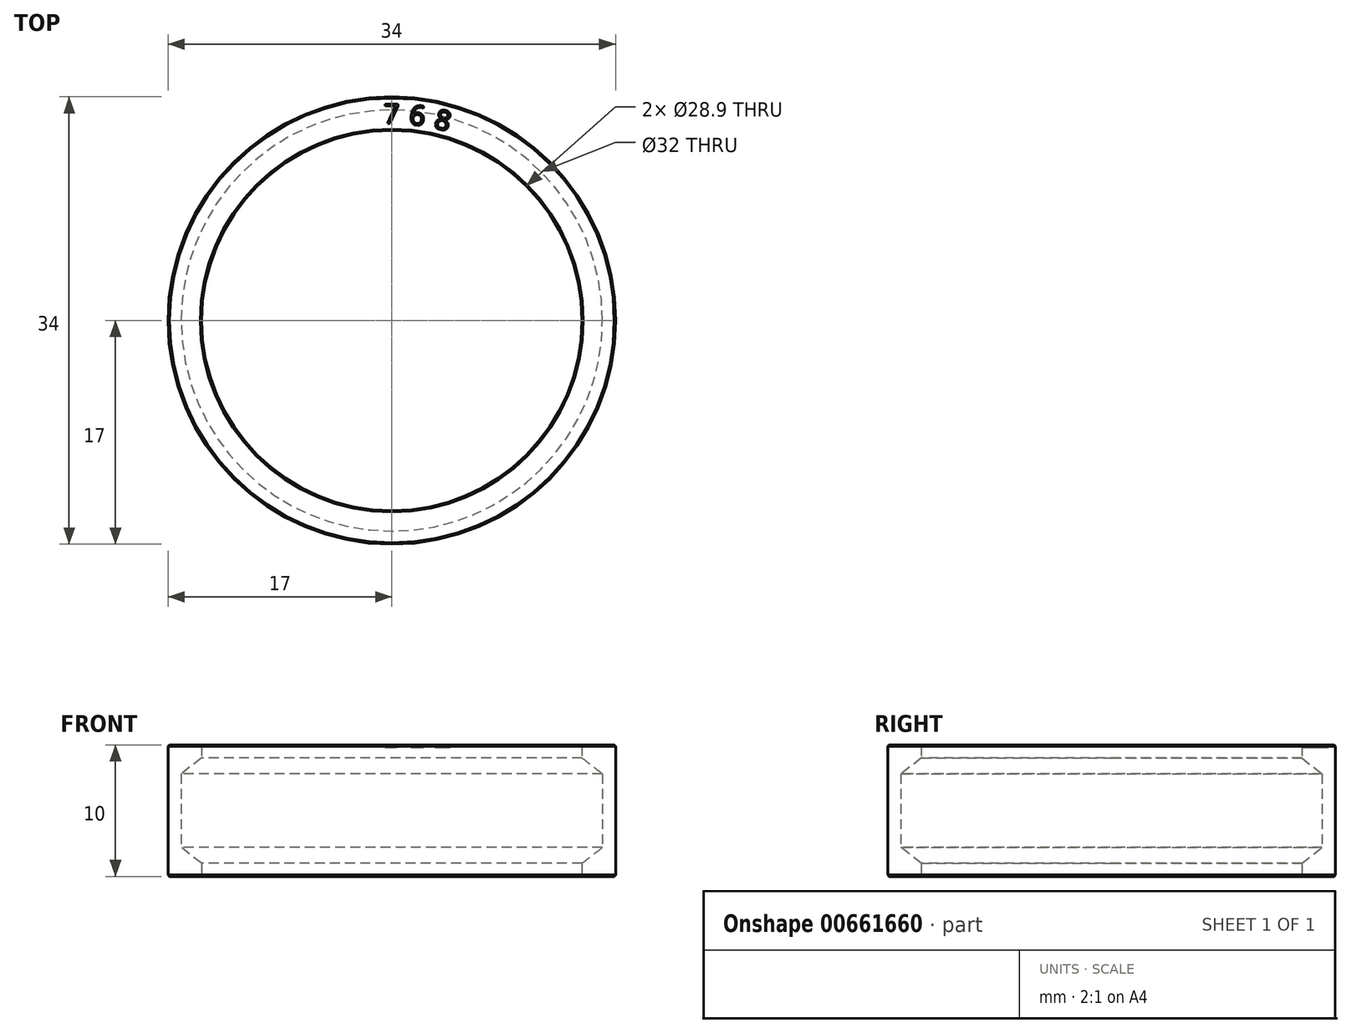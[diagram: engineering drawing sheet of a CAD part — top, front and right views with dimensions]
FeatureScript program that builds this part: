
annotation { "Feature Type Name" : "Feature", "Feature Type Description" : "" }
export const myFeature = defineFeature(function(context is Context, id is Id, definition is map)
    precondition{}
    {
        {
            var Q0;
            Q0=qCreatedBy(makeId("Top.planeOp"),FACE);
            var sketch = newSketch(context, id + "F0", { "sketchPlane" : qUnion([Q0])});
            skCircle(sketch, "E0", {"center": v(0, 0) * mm, "radius": 14.45 * mm});
            skCircle(sketch, "E1", {"center": v(0, 0) * mm, "radius": 17 * mm});
            skCircle(sketch, "E2", {"center": v(0, 0) * mm, "radius": 16 * mm});
            skSolve(sketch);
        }
        {
            var Q0;
            Q0=makeQuery(id+"F0.imprint","IMPRINT",FACE,{"disambiguationData":[TD([[makeQuery(id+"F0.imprint","IMPRINT",EDGE,{"derivedFrom":sQuery(id+"F0.wireOp",EDGE,"E0")}),-1.0]])]});
            var Q1;
            Q1=makeQuery(id+"F0.imprint","IMPRINT",FACE,{"disambiguationData":[TD([[makeQuery(id+"F0.imprint","IMPRINT",EDGE,{"derivedFrom":sQuery(id+"F0.wireOp",EDGE,"E1")}),1.0]])]});
            extrude(context, id + "F1", {"entities" : qUnion([Q0, Q1]), "endBound" : BoundingType.SYMMETRIC, "depth" : 10 * mm, "offsetDistance" : 25 * mm});
        }
        {
            var Q0;
            Q0=makeQuery(id+"F0.imprint","IMPRINT",FACE,{"disambiguationData":[TD([[makeQuery(id+"F0.imprint","IMPRINT",EDGE,{"derivedFrom":sQuery(id+"F0.wireOp",EDGE,"E0")}),-1.0]])]});
            var Q1;
            Q1=makeQuery(id+"F1.opExtrude","CAP_FACE",FACE,{"disambiguationData":[OSD([sQuery(id+"F0.wireOp",EDGE,"E0"),sQuery(id+"F0.wireOp",EDGE,"E1")])],"isStart":false});
            var Q2;
            Q2=makeQuery(id+"F1.opExtrude","CAP_FACE",FACE,{"disambiguationData":[OSD([sQuery(id+"F0.wireOp",EDGE,"E0"),sQuery(id+"F0.wireOp",EDGE,"E1")])],"isStart":true});
            extrude(context, id + "F2", {"entities" : qUnion([Q0]), "operationType" : NewBodyOperationType.REMOVE, "endBound" : BoundingType.UP_TO_SURFACE, "depth" : 25 * mm, "endBoundEntityFace" : qUnion([Q1]), "hasOffset" : true, "offsetDistance" : 1 * mm, "hasSecondDirection" : true, "secondDirectionBound" : SecondDirectionBoundingType.UP_TO_SURFACE, "secondDirectionOppositeDirection" : true, "secondDirectionDepth" : 25 * mm, "secondDirectionBoundEntityFace" : qUnion([Q2]), "hasSecondDirectionOffset" : true, "secondDirectionOffsetDistance" : 1 * mm});
        }
        {
            var Q0;
            Q0=makeQuery(id+"F2.boolean.opBoolean","COPY",EDGE,{"derivedFrom":makeQuery(id+"F2.opExtrude","CAP_EDGE",EDGE,{"disambiguationData":[OSD([sQuery(id+"F0.wireOp",EDGE,"E2")])],"isStart":true})});
            var Q1;
            Q1=makeQuery(id+"F2.boolean.opBoolean","COPY",EDGE,{"derivedFrom":makeQuery(id+"F2.opExtrude","CAP_EDGE",EDGE,{"disambiguationData":[OSD([sQuery(id+"F0.wireOp",EDGE,"E2")])],"isStart":false})});
            chamfer(context, id + "F3", {"entities" : qUnion([Q0, Q1]), "chamferType" : ChamferType.TWO_OFFSETS, "width1" : 1.55 * mm, "oppositeDirection" : false, "width2" : 1.2 * mm, "tangentPropagation" : true});
        }
        {
            var Q0;
            Q0=makeQuery(id+"F1.opExtrude","CAP_EDGE",EDGE,{"disambiguationData":[OSD([sQuery(id+"F0.wireOp",EDGE,"E1")])],"isStart":false});
            var Q1;
            Q1=makeQuery(id+"F1.opExtrude","CAP_EDGE",EDGE,{"disambiguationData":[OSD([sQuery(id+"F0.wireOp",EDGE,"E1")])],"isStart":true});
            chamfer(context, id + "F4", {"entities" : qUnion([Q0, Q1]), "width" : 0.1 * mm, "tangentPropagation" : true});
        }
        {
            var Q0;
            Q0=makeQuery(id+"F1.opExtrude","CAP_FACE",FACE,{"disambiguationData":[OSD([sQuery(id+"F0.wireOp",EDGE,"E0"),sQuery(id+"F0.wireOp",EDGE,"E1")])],"isStart":false});
            var sketch = newSketch(context, id + "F5", { "sketchPlane" : qUnion([Q0])});
            skPoint(sketch, "E3.0", {"position": v(0, 0) * mm});
            skCircle(sketch, "E4.0", {"center": v(0, 0) * mm, "radius": 14.45 * mm});
            skCircle(sketch, "E5.0", {"center": v(0, 0) * mm, "radius": 17 * mm});
            skCircle(sketch, "E6", {"center": v(0, 0) * mm, "radius": 14.97 * mm, "construction": true});
            skCircle(sketch, "E7.0", {"center": v(0, 0) * mm, "radius": 16.9 * mm});
            skCircle(sketch, "E8.cCircle", {"center": v(0, 0) * mm, "radius": 14.95 * mm, "construction": true});
            skLineSegment(sketch, "E8.0", {"start": v(-3.72, -14.5) * mm, "end": v(-5.51, -13.92) * mm});
            skLineSegment(sketch, "E8.1", {"start": v(-5.51, -13.92) * mm, "end": v(-7.21, -13.12) * mm});
            skLineSegment(sketch, "E8.2", {"start": v(-7.21, -13.12) * mm, "end": v(-8.8, -12.12) * mm});
            skLineSegment(sketch, "E8.3", {"start": v(-8.8, -12.12) * mm, "end": v(-10.25, -10.92) * mm});
            skLineSegment(sketch, "E8.4", {"start": v(-10.25, -10.92) * mm, "end": v(-11.54, -9.55) * mm});
            skLineSegment(sketch, "E8.5", {"start": v(-11.54, -9.55) * mm, "end": v(-12.64, -8.02) * mm});
            skLineSegment(sketch, "E8.6", {"start": v(-12.64, -8.02) * mm, "end": v(-13.55, -6.38) * mm});
            skLineSegment(sketch, "E8.7", {"start": v(-13.55, -6.38) * mm, "end": v(-14.24, -4.63) * mm});
            skLineSegment(sketch, "E8.8", {"start": v(-14.24, -4.63) * mm, "end": v(-14.7, -2.8) * mm});
            skLineSegment(sketch, "E8.9", {"start": v(-14.7, -2.8) * mm, "end": v(-14.95, -0.94) * mm});
            skLineSegment(sketch, "E8.10", {"start": v(-14.95, -0.94) * mm, "end": v(-14.95, 0.94) * mm});
            skLineSegment(sketch, "E8.11", {"start": v(-14.95, 0.94) * mm, "end": v(-14.7, 2.8) * mm});
            skLineSegment(sketch, "E8.12", {"start": v(-14.7, 2.8) * mm, "end": v(-14.24, 4.63) * mm});
            skLineSegment(sketch, "E8.13", {"start": v(-14.24, 4.63) * mm, "end": v(-13.55, 6.38) * mm});
            skLineSegment(sketch, "E8.14", {"start": v(-13.55, 6.38) * mm, "end": v(-12.64, 8.02) * mm});
            skLineSegment(sketch, "E8.15", {"start": v(-12.64, 8.02) * mm, "end": v(-11.54, 9.55) * mm});
            skLineSegment(sketch, "E8.16", {"start": v(-11.54, 9.55) * mm, "end": v(-10.25, 10.92) * mm});
            skLineSegment(sketch, "E8.17", {"start": v(-10.25, 10.92) * mm, "end": v(-8.8, 12.12) * mm});
            skLineSegment(sketch, "E8.18", {"start": v(-8.8, 12.12) * mm, "end": v(-7.21, 13.12) * mm});
            skLineSegment(sketch, "E8.19", {"start": v(-7.21, 13.12) * mm, "end": v(-5.51, 13.92) * mm});
            skLineSegment(sketch, "E8.20", {"start": v(-5.51, 13.92) * mm, "end": v(-3.72, 14.5) * mm});
            skLineSegment(sketch, "E8.21", {"start": v(-3.72, 14.5) * mm, "end": v(-1.88, 14.86) * mm});
            skLineSegment(sketch, "E8.22", {"start": v(-1.88, 14.86) * mm, "end": v(0, 14.97) * mm});
            skLineSegment(sketch, "E8.23", {"start": v(0, 14.97) * mm, "end": v(1.88, 14.86) * mm});
            skLineSegment(sketch, "E8.24", {"start": v(1.88, 14.86) * mm, "end": v(3.72, 14.5) * mm});
            skLineSegment(sketch, "E8.25", {"start": v(3.72, 14.5) * mm, "end": v(5.51, 13.92) * mm});
            skLineSegment(sketch, "E8.26", {"start": v(5.51, 13.92) * mm, "end": v(7.21, 13.12) * mm});
            skLineSegment(sketch, "E8.27", {"start": v(7.21, 13.12) * mm, "end": v(8.8, 12.12) * mm});
            skLineSegment(sketch, "E8.28", {"start": v(8.8, 12.12) * mm, "end": v(10.25, 10.92) * mm});
            skLineSegment(sketch, "E8.29", {"start": v(10.25, 10.92) * mm, "end": v(11.54, 9.55) * mm});
            skLineSegment(sketch, "E8.30", {"start": v(11.54, 9.55) * mm, "end": v(12.64, 8.02) * mm});
            skLineSegment(sketch, "E8.31", {"start": v(12.64, 8.02) * mm, "end": v(13.55, 6.38) * mm});
            skLineSegment(sketch, "E8.32", {"start": v(13.55, 6.38) * mm, "end": v(14.24, 4.63) * mm});
            skLineSegment(sketch, "E8.33", {"start": v(14.24, 4.63) * mm, "end": v(14.7, 2.8) * mm});
            skLineSegment(sketch, "E8.34", {"start": v(14.7, 2.8) * mm, "end": v(14.95, 0.94) * mm});
            skLineSegment(sketch, "E8.35", {"start": v(14.95, 0.94) * mm, "end": v(14.95, -0.94) * mm});
            skLineSegment(sketch, "E8.36", {"start": v(14.95, -0.94) * mm, "end": v(14.7, -2.8) * mm});
            skLineSegment(sketch, "E8.37", {"start": v(14.7, -2.8) * mm, "end": v(14.24, -4.63) * mm});
            skLineSegment(sketch, "E8.38", {"start": v(14.24, -4.63) * mm, "end": v(13.55, -6.38) * mm});
            skLineSegment(sketch, "E8.39", {"start": v(13.55, -6.38) * mm, "end": v(12.64, -8.02) * mm});
            skLineSegment(sketch, "E8.40", {"start": v(12.64, -8.02) * mm, "end": v(11.54, -9.55) * mm});
            skLineSegment(sketch, "E8.41", {"start": v(11.54, -9.55) * mm, "end": v(10.25, -10.92) * mm});
            skLineSegment(sketch, "E8.42", {"start": v(10.25, -10.92) * mm, "end": v(8.8, -12.12) * mm});
            skLineSegment(sketch, "E8.43", {"start": v(8.8, -12.12) * mm, "end": v(7.21, -13.12) * mm});
            skLineSegment(sketch, "E8.44", {"start": v(7.21, -13.12) * mm, "end": v(5.51, -13.92) * mm});
            skLineSegment(sketch, "E8.45", {"start": v(5.51, -13.92) * mm, "end": v(3.72, -14.5) * mm});
            skLineSegment(sketch, "E8.46", {"start": v(3.72, -14.5) * mm, "end": v(1.88, -14.86) * mm});
            skLineSegment(sketch, "E8.47", {"start": v(1.88, -14.86) * mm, "end": v(0, -14.97) * mm});
            skLineSegment(sketch, "E8.48", {"start": v(0, -14.97) * mm, "end": v(-1.88, -14.86) * mm});
            skLineSegment(sketch, "E8.49", {"start": v(-1.88, -14.86) * mm, "end": v(-3.72, -14.5) * mm});
            skPoint(sketch, "E8.0.midPoint", {"position": v(-4.62, -14.21) * mm});
            skLineSegment(sketch, "E9", {"start": v(0, 0) * mm, "end": v(0, 14.97) * mm, "construction": true});
            skLineSegment(sketch, "E10", {"start": v(0, 0) * mm, "end": v(1.88, 14.86) * mm, "construction": true});
            skLineSegment(sketch, "E11", {"start": v(0, 0) * mm, "end": v(3.72, 14.5) * mm, "construction": true});
            skText(sketch, "E12", { "text": "7", "fontName": "OpenSans-Regular.ttf"});
            skText(sketch, "E13", { "text": "8", "fontName": "OpenSans-Regular.ttf"});
            skText(sketch, "E14", { "text": "6", "fontName": "OpenSans-Regular.ttf"});
            skLineSegment(sketch, "E15", {"start": v(0, 0) * mm, "end": v(7.21, 13.12) * mm, "construction": true});
            skText(sketch, "E16", { "text": "C", "fontName": "OpenSans-Regular.ttf"});
            const initialGuessF5  = {"E12": [-0.00061, 0.01497, 1, 0, 0.0015], "E13": [0.00313, 0.01466, 0.96858, -0.24869, 0.0015], "E14": [0.00127, 0.01493, 0.99211, -0.12533, 0.0015], "E16": [0.0066, 0.01346, 0.8763, -0.48175, 0.0015]};
            skSetInitialGuess(sketch, initialGuessF5);
            skSolve(sketch);
        }
        {
            var Q0;
            Q0=makeQuery(id+"F5.imprint","IMPRINT",FACE,{"disambiguationData":[TD([[makeQuery(id+"F5.imprint","IMPRINT",EDGE,{"derivedFrom":sQuery(id+"F5.wireOp",EDGE,"E14.sketch_text.stroke-0")}),-1.0]])]});
            var Q1;
            Q1=makeQuery(id+"F5.imprint","IMPRINT",FACE,{"disambiguationData":[TD([[makeQuery(id+"F5.imprint","IMPRINT",EDGE,{"derivedFrom":sQuery(id+"F5.wireOp",EDGE,"E12.sketch_text.stroke-0")}),-1.0]])]});
            var Q2;
            Q2=makeQuery(id+"F5.imprint","IMPRINT",FACE,{"disambiguationData":[TD([[makeQuery(id+"F5.imprint","IMPRINT",EDGE,{"derivedFrom":sQuery(id+"F5.wireOp",EDGE,"E13.sketch_text.stroke-0")}),-1.0]])]});
            extrude(context, id + "F6", {"entities" : qUnion([Q0, Q1, Q2]), "operationType" : NewBodyOperationType.REMOVE, "oppositeDirection" : true, "depth" : 0.2 * mm, "offsetDistance" : 25 * mm});
        }
        {
            var Q0;
            Q0=makeQuery(id+"F1.opExtrude","CAP_EDGE",EDGE,{"disambiguationData":[OSD([sQuery(id+"F0.wireOp",EDGE,"E0")])],"isStart":false});
            var Q1;
            Q1=makeQuery(id+"F1.opExtrude","CAP_EDGE",EDGE,{"disambiguationData":[OSD([sQuery(id+"F0.wireOp",EDGE,"E0")])],"isStart":true});
            chamfer(context, id + "F7", {"entities" : qUnion([Q0, Q1]), "width" : 0.1 * mm, "tangentPropagation" : true});
        }
    });
